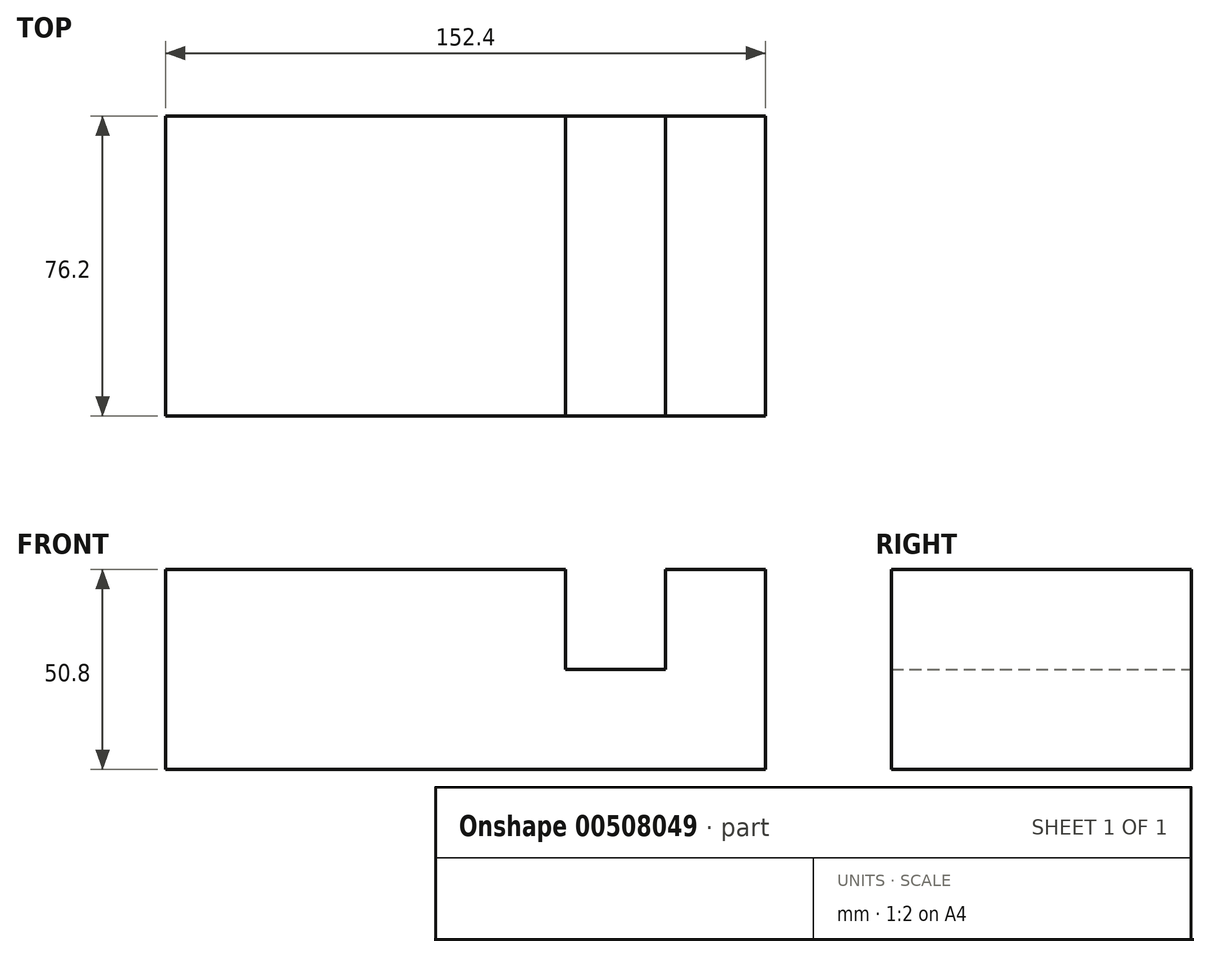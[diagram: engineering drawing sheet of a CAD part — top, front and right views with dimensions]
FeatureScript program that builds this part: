
annotation { "Feature Type Name" : "Feature", "Feature Type Description" : "" }
export const myFeature = defineFeature(function(context is Context, id is Id, definition is map)
    precondition{}
    {
        {
            var Q0;
            Q0=qCreatedBy(makeId("Front.planeOp"),FACE);
            var sketch = newSketch(context, id + "F0", { "sketchPlane" : qUnion([Q0])});
            skLineSegment(sketch, "E0", {"start": v(-123.12, 8.26) * mm, "end": v(-123.12, -42.54) * mm});
            skLineSegment(sketch, "E1", {"start": v(-123.12, -42.54) * mm, "end": v(29.28, -42.54) * mm});
            skLineSegment(sketch, "E2", {"start": v(29.28, -42.54) * mm, "end": v(29.28, 8.26) * mm});
            skLineSegment(sketch, "E3", {"start": v(29.28, 8.26) * mm, "end": v(3.88, 8.26) * mm});
            skLineSegment(sketch, "E4", {"start": v(3.88, 8.26) * mm, "end": v(3.88, -17.14) * mm});
            skLineSegment(sketch, "E5", {"start": v(3.88, -17.14) * mm, "end": v(-21.52, -17.14) * mm});
            skLineSegment(sketch, "E6", {"start": v(-21.52, -17.14) * mm, "end": v(-21.52, 8.26) * mm});
            skLineSegment(sketch, "E7", {"start": v(-21.52, 8.26) * mm, "end": v(-123.12, 8.26) * mm});
            skSolve(sketch);
        }
        {
            var Q0;
            Q0=makeQuery(id+"F0.imprint","IMPRINT",FACE,{"disambiguationData":[TD([[makeQuery(id+"F0.imprint","IMPRINT",EDGE,{"derivedFrom":sQuery(id+"F0.wireOp",EDGE,"E0")}),1.0]])]});
            extrude(context, id + "F1", {"entities" : qUnion([Q0]), "depth" : 76.2 * mm});
        }
    });
